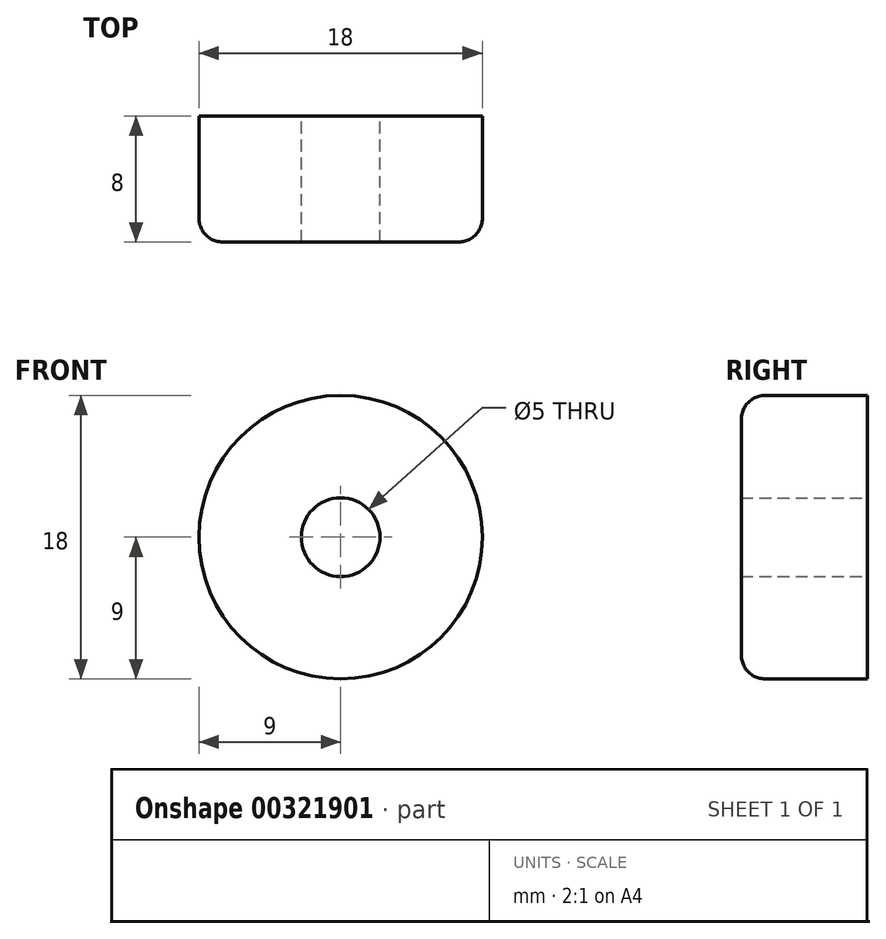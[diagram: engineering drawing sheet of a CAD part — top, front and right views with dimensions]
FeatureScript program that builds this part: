
annotation { "Feature Type Name" : "Feature", "Feature Type Description" : "" }
export const myFeature = defineFeature(function(context is Context, id is Id, definition is map)
    precondition{}
    {
        {
            var Q0;
            Q0=qCreatedBy(makeId("Front.planeOp"),FACE);
            var sketch = newSketch(context, id + "F0", { "sketchPlane" : qUnion([Q0])});
            skCircle(sketch, "E0", {"center": v(0, 0) * mm, "radius": 9 * mm});
            skCircle(sketch, "E1", {"center": v(0, 0) * mm, "radius": 2.5 * mm});
            skSolve(sketch);
        }
        {
            var Q0;
            Q0=makeQuery(id+"F0.imprint","IMPRINT",FACE,{"disambiguationData":[TD([[makeQuery(id+"F0.imprint","IMPRINT",EDGE,{"derivedFrom":sQuery(id+"F0.wireOp",EDGE,"E0")}),1.0]])]});
            var Q1;
            Q1=sQuery(id+"F0.wireOp",EDGE,"E0");
            var Q2;
            Q2=sQuery(id+"F0.wireOp",EDGE,"E1");
            extrude(context, id + "F1", {"entities" : qUnion([Q0]), "surfaceEntities" : qUnion([Q1, Q2]), "depth" : 8 * mm});
        }
        {
            var Q0;
            Q0=makeQuery(id+"F1.opExtrude","CAP_EDGE",EDGE,{"disambiguationData":[OSD([sQuery(id+"F0.wireOp",EDGE,"E0")])],"isStart":false});
            fillet(context, id + "F2", {"entities" : qUnion([Q0]), "radius" : 1.5 * mm, "tangentPropagation" : true, "allowEdgeOverflow" : false});
        }
    });
